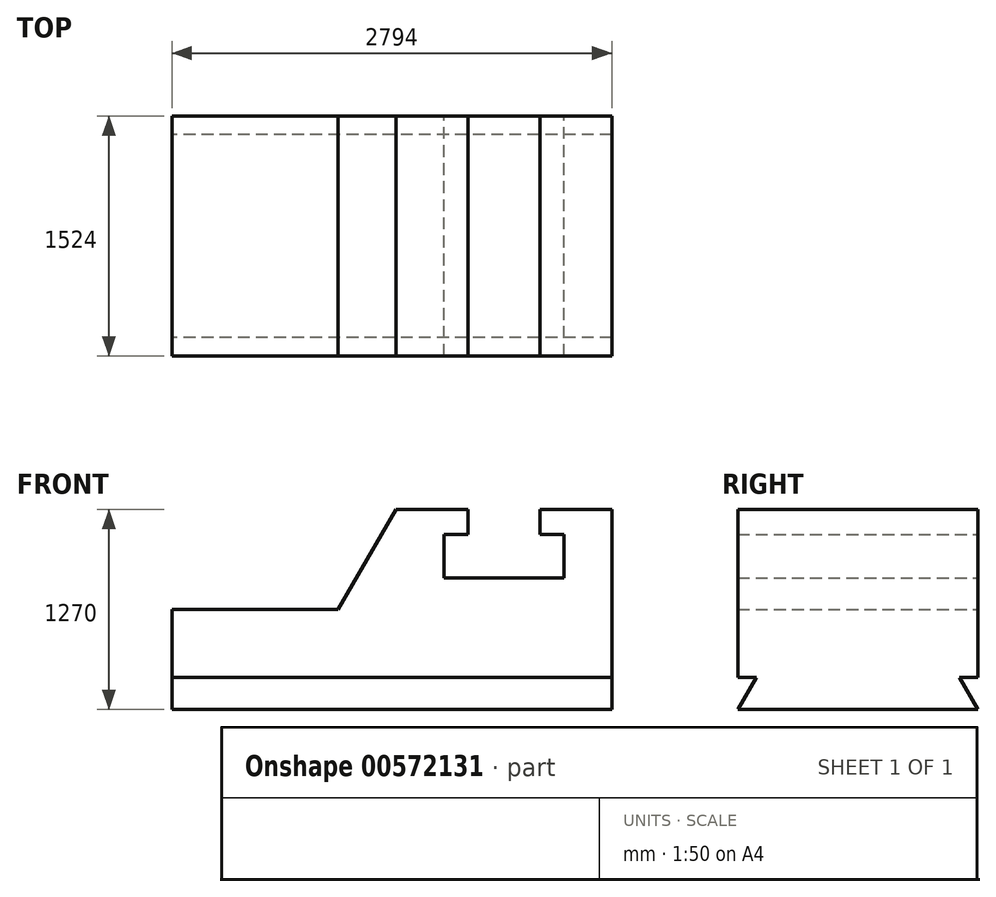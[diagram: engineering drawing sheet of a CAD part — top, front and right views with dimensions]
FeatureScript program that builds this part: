
annotation { "Feature Type Name" : "Feature", "Feature Type Description" : "" }
export const myFeature = defineFeature(function(context is Context, id is Id, definition is map)
    precondition{}
    {
        {
            var Q0;
            Q0=qCreatedBy(makeId("Front.planeOp"),FACE);
            var sketch = newSketch(context, id + "F0", { "sketchPlane" : qUnion([Q0])});
            skLineSegment(sketch, "E0", {"start": v(-1327.06, -659.38) * mm, "end": v(1466.94, -659.38) * mm});
            skLineSegment(sketch, "E1", {"start": v(1466.94, -659.38) * mm, "end": v(1466.94, 610.62) * mm});
            skLineSegment(sketch, "E2", {"start": v(1466.94, 610.62) * mm, "end": v(1009.74, 610.62) * mm});
            skLineSegment(sketch, "E3", {"start": v(1009.74, 610.62) * mm, "end": v(1009.74, 451.87) * mm});
            skLineSegment(sketch, "E4", {"start": v(1009.74, 451.87) * mm, "end": v(1162.14, 451.87) * mm});
            skLineSegment(sketch, "E5", {"start": v(1162.14, 451.87) * mm, "end": v(1162.14, 176.7) * mm});
            skLineSegment(sketch, "E6", {"start": v(1162.14, 176.7) * mm, "end": v(400.14, 176.7) * mm});
            skLineSegment(sketch, "E7", {"start": v(400.14, 176.7) * mm, "end": v(400.14, 451.87) * mm});
            skLineSegment(sketch, "E8", {"start": v(400.14, 451.87) * mm, "end": v(552.54, 451.87) * mm});
            skLineSegment(sketch, "E9", {"start": v(552.54, 451.87) * mm, "end": v(552.54, 610.62) * mm});
            skLineSegment(sketch, "E10", {"start": v(552.54, 610.62) * mm, "end": v(95.34, 610.62) * mm});
            skLineSegment(sketch, "E11", {"start": v(-1327.06, -659.38) * mm, "end": v(-1327.06, -24.38) * mm});
            skLineSegment(sketch, "E12", {"start": v(-1327.06, -24.38) * mm, "end": v(-271.27, -24.38) * mm});
            skLineSegment(sketch, "E13", {"start": v(-271.27, -24.38) * mm, "end": v(95.34, 610.62) * mm});
            skLineSegment(sketch, "E14", {"start": v(-1327.06, -456.18) * mm, "end": v(1466.94, -456.18) * mm});
            skSolve(sketch);
        }
        {
            var Q0;
            {var subQ0=sQuery(id+"F0.wireOp",EDGE,"E2");Q0=makeQuery(id+"F0.imprint","IMPRINT",FACE,{"disambiguationData":[TD([[makeQuery(id+"F0.imprint","IMPRINT",EDGE,{"derivedFrom":subQ0}),1.0]])]});}
            var Q1;
            {var subQ0=sQuery(id+"F0.wireOp",EDGE,"E0");Q1=makeQuery(id+"F0.imprint","IMPRINT",FACE,{"disambiguationData":[TD([[makeQuery(id+"F0.imprint","IMPRINT",EDGE,{"derivedFrom":subQ0}),1.0]])]});}
            extrude(context, id + "F1", {"entities" : qUnion([Q0, Q1]), "depth" : 1524 * mm, "offsetDistance" : 25.4 * mm});
        }
        {
            var Q0;
            Q0=makeQuery(id+"F1.opExtrude","SWEPT_FACE",FACE,{"disambiguationData":[OSD([sQuery(id+"F0.wireOp",EDGE,"E11")])]});
            var sketch = newSketch(context, id + "F2", { "sketchPlane" : qUnion([Q0])});
            skLineSegment(sketch, "E15", {"start": v(0, -456.18) * mm, "end": v(1524, -456.18) * mm});
            skLineSegment(sketch, "E16", {"start": v(0, -659.38) * mm, "end": v(117.32, -456.18) * mm});
            skLineSegment(sketch, "E17", {"start": v(1524, -659.38) * mm, "end": v(1406.68, -456.18) * mm});
            skSolve(sketch);
        }
        {
            var Q0;
            {var subQ4=sQuery(id+"F2.wireOp",EDGE,"E16");Q0=makeQuery(id+"F2.imprint","IMPRINT",FACE,{"disambiguationData":[TD([[makeQuery(id+"F2.imprint","IMPRINT",EDGE,{"derivedFrom":subQ4}),1.0]])]});}
            var Q1;
            {var subQ4=sQuery(id+"F2.wireOp",EDGE,"E17");Q1=makeQuery(id+"F2.imprint","IMPRINT",FACE,{"disambiguationData":[TD([[makeQuery(id+"F2.imprint","IMPRINT",EDGE,{"derivedFrom":subQ4}),-1.0]])]});}
            extrude(context, id + "F3", {"entities" : qUnion([Q0, Q1]), "operationType" : NewBodyOperationType.REMOVE, "oppositeDirection" : true, "depth" : 2794 * mm, "offsetDistance" : 25.4 * mm});
        }
    });
